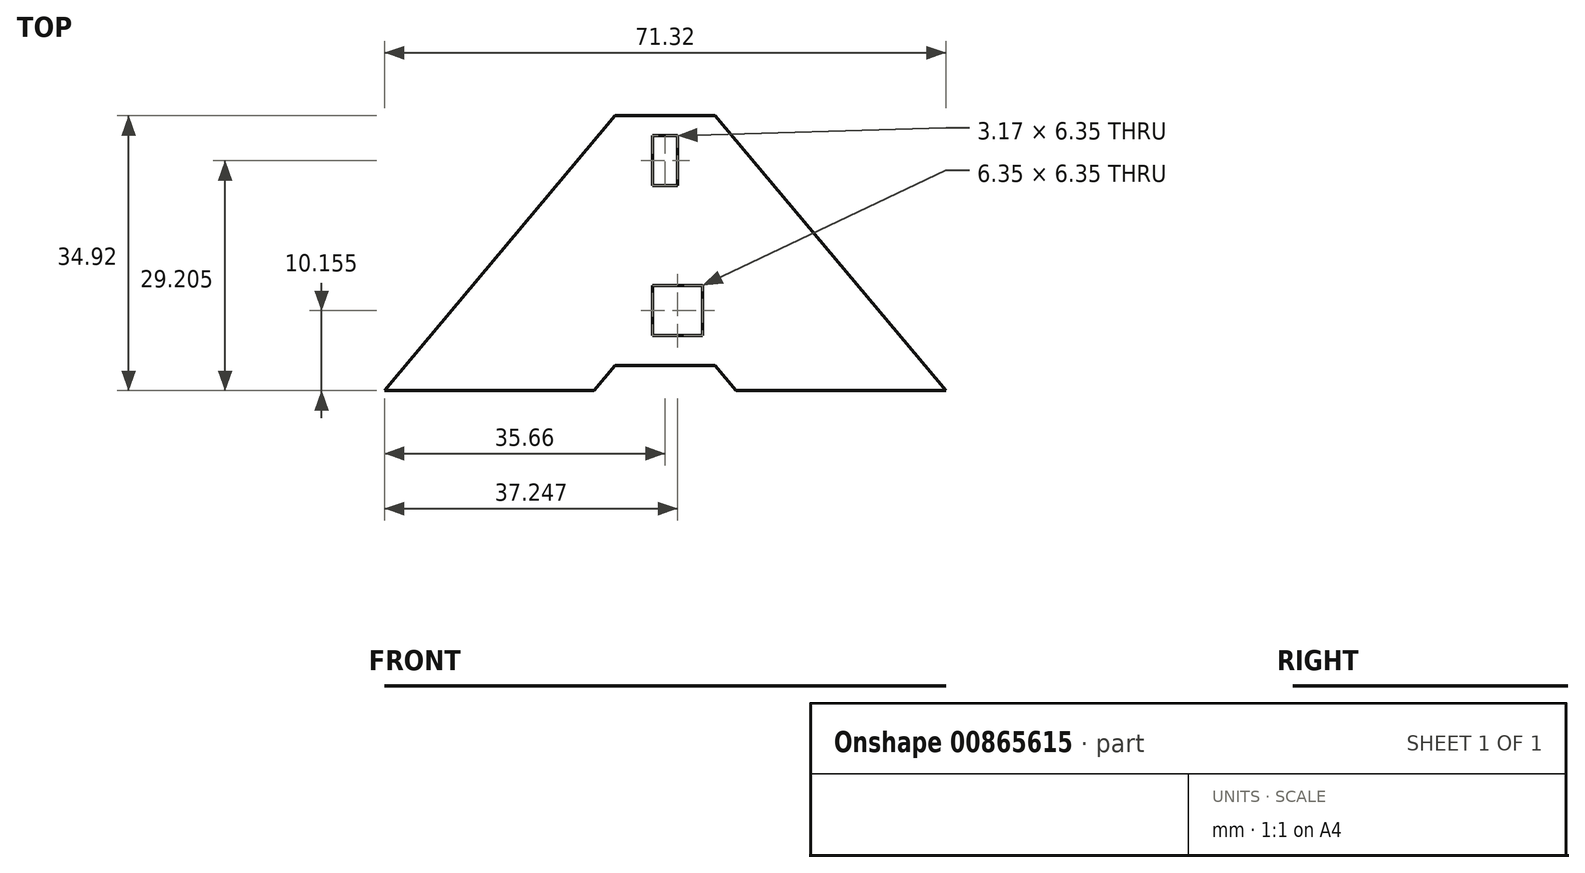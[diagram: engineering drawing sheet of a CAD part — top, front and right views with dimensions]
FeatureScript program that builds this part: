
annotation { "Feature Type Name" : "Feature", "Feature Type Description" : "" }
export const myFeature = defineFeature(function(context is Context, id is Id, definition is map)
    precondition{}
    {
        {
            var Q0;
            Q0=qCreatedBy(makeId("Top.planeOp"),FACE);
            var sketch = newSketch(context, id + "F0", { "sketchPlane" : qUnion([Q0])});
            skLineSegment(sketch, "E0", {"start": v(-6.35, 0) * mm, "end": v(6.35, 0) * mm});
            skLineSegment(sketch, "E1", {"start": v(6.35, 0) * mm, "end": v(35.66, -34.93) * mm});
            skLineSegment(sketch, "E2", {"start": v(35.66, -34.93) * mm, "end": v(9.01, -34.93) * mm});
            skLineSegment(sketch, "E3", {"start": v(9.01, -34.92) * mm, "end": v(6.35, -31.75) * mm});
            skLineSegment(sketch, "E4", {"start": v(6.35, -31.75) * mm, "end": v(-6.35, -31.75) * mm});
            skLineSegment(sketch, "E5", {"start": v(-6.35, -31.75) * mm, "end": v(-9.01, -34.93) * mm});
            skLineSegment(sketch, "E6", {"start": v(-9.01, -34.93) * mm, "end": v(-35.66, -34.93) * mm});
            skLineSegment(sketch, "E7", {"start": v(-35.66, -34.93) * mm, "end": v(-6.35, 0) * mm});
            skLineSegment(sketch, "E8", {"start": v(-35.66, -34.93) * mm, "end": v(35.66, -34.93) * mm, "construction": true});
            skLineSegment(sketch, "E9", {"start": v(0, 0) * mm, "end": v(0, -31.75) * mm, "construction": true});
            skLineSegment(sketch, "E10.bottom", {"start": v(-1.59, -2.54) * mm, "end": v(1.59, -2.54) * mm});
            skLineSegment(sketch, "E10.top", {"start": v(-1.59, -8.89) * mm, "end": v(1.59, -8.89) * mm});
            skLineSegment(sketch, "E10.left", {"start": v(-1.59, -2.54) * mm, "end": v(-1.59, -8.89) * mm});
            skLineSegment(sketch, "E10.right", {"start": v(1.59, -2.54) * mm, "end": v(1.59, -8.89) * mm});
            skLineSegment(sketch, "E11.bottom", {"start": v(-1.59, -21.59) * mm, "end": v(4.76, -21.59) * mm});
            skLineSegment(sketch, "E11.top", {"start": v(-1.59, -27.94) * mm, "end": v(4.76, -27.94) * mm});
            skLineSegment(sketch, "E11.left", {"start": v(-1.59, -21.59) * mm, "end": v(-1.59, -27.94) * mm});
            skLineSegment(sketch, "E11.right", {"start": v(4.76, -21.59) * mm, "end": v(4.76, -27.94) * mm});
            skPoint(sketch, "E12", {"position": v(0, -2.54) * mm});
            skLineSegment(sketch, "E13", {"start": v(1.59, -21.59) * mm, "end": v(1.59, -27.94) * mm});
            skLineSegment(sketch, "E14", {"start": v(1.59, -20.8) * mm, "end": v(-1.59, -20.8) * mm, "construction": true});
            skLineSegment(sketch, "E15", {"start": v(-1.59, -20.8) * mm, "end": v(-1.59, -21.59) * mm, "construction": true});
            skLineSegment(sketch, "E16", {"start": v(1.59, -20.8) * mm, "end": v(1.59, -21.59) * mm, "construction": true});
            skPoint(sketch, "E17", {"position": v(0, -20.8) * mm});
            skSolve(sketch);
        }
        {
            var Q0;
            Q0=makeQuery(id+"F0.imprint","IMPRINT",FACE,{"disambiguationData":[TD([[makeQuery(id+"F0.imprint","IMPRINT",EDGE,{"derivedFrom":sQuery(id+"F0.wireOp",EDGE,"E0")}),-1.0]])]});
            extrude(context, id + "F1", {"entities" : qUnion([Q0]), "depth" : 1 / 203.2 * mm, "offsetDistance" : 25.4 * mm});
        }
    });
